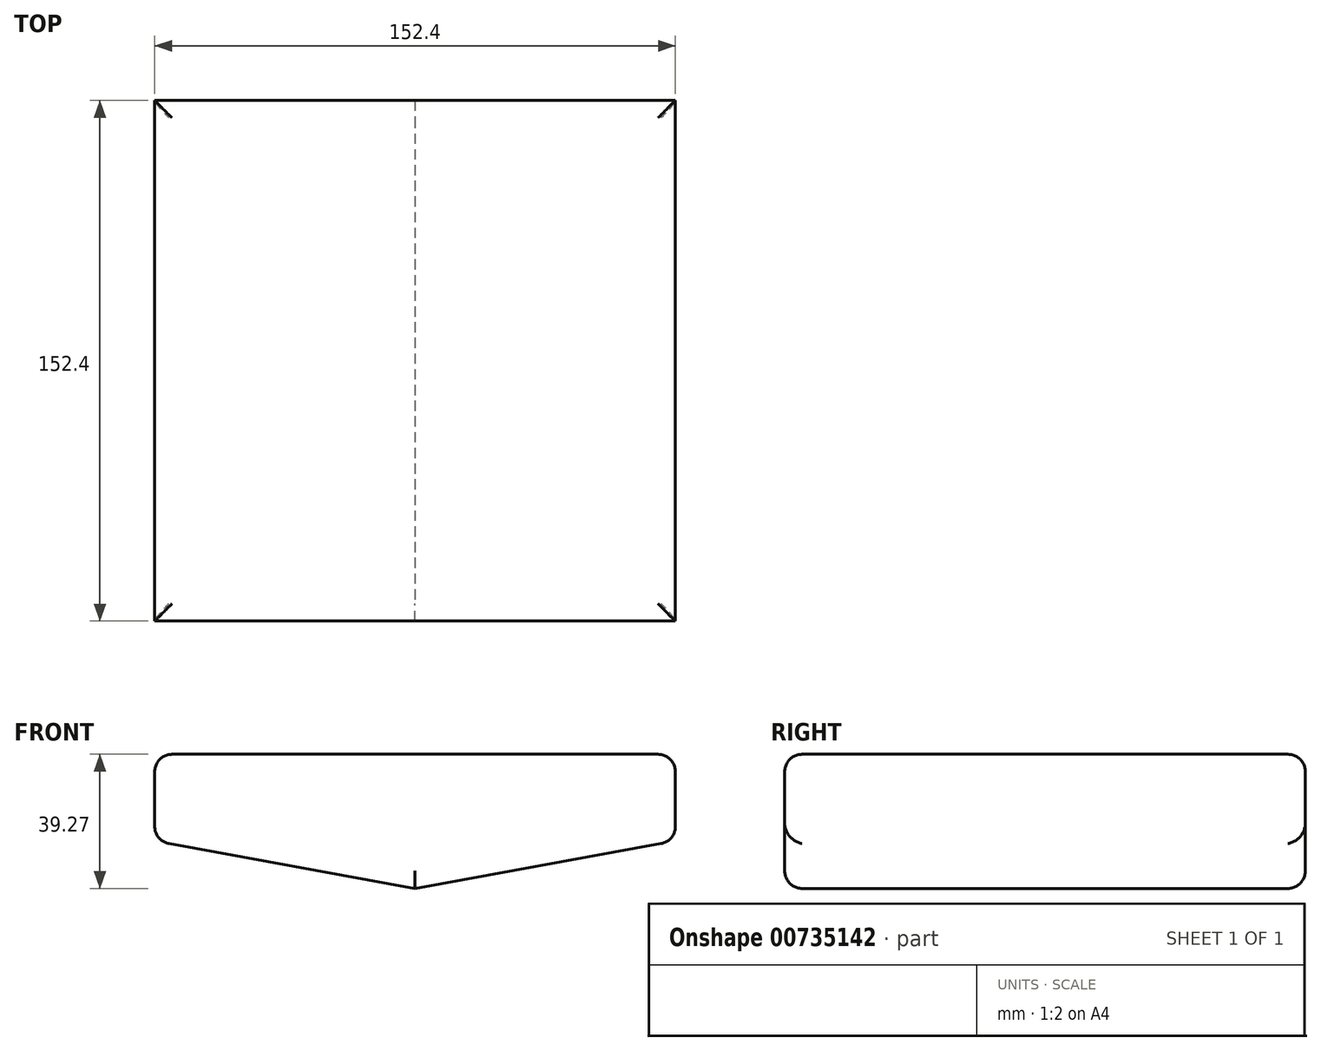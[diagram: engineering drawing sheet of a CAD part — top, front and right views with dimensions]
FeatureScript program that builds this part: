
annotation { "Feature Type Name" : "Feature", "Feature Type Description" : "" }
export const myFeature = defineFeature(function(context is Context, id is Id, definition is map)
    precondition{}
    {
        {
            var Q0;
            Q0=qCreatedBy(makeId("Front.planeOp"),FACE);
            var sketch = newSketch(context, id + "F0", { "sketchPlane" : qUnion([Q0])});
            skLineSegment(sketch, "E0", {"start": v(0, 0) * mm, "end": v(-76.2, 0) * mm});
            skLineSegment(sketch, "E1", {"start": v(0, 0) * mm, "end": v(76.2, 0) * mm});
            skLineSegment(sketch, "E2", {"start": v(76.2, 0) * mm, "end": v(76.2, -25.4) * mm});
            skLineSegment(sketch, "E3", {"start": v(-76.2, 0) * mm, "end": v(-76.2, -25.4) * mm});
            skLineSegment(sketch, "E4", {"start": v(-76.2, -25.4) * mm, "end": v(0, -39.27) * mm});
            skLineSegment(sketch, "E5", {"start": v(0, -39.27) * mm, "end": v(76.2, -25.4) * mm});
            skSolve(sketch);
        }
        {
            var Q0;
            Q0=makeQuery(id+"F0.imprint","IMPRINT",FACE,{"disambiguationData":[TD([[makeQuery(id+"F0.imprint","IMPRINT",EDGE,{"derivedFrom":sQuery(id+"F0.wireOp",EDGE,"E0")}),1.0]])]});
            extrude(context, id + "F1", {"entities" : qUnion([Q0]), "oppositeDirection" : true, "depth" : 152.4 * mm, "offsetDistance" : 25.4 * mm});
        }
        {
            var Q0;
            Q0=makeQuery(id+"F1.opExtrude","SWEPT_FACE",FACE,{"disambiguationData":[OSD([sQuery(id+"F0.wireOp",EDGE,"E0"),sQuery(id+"F0.wireOp",EDGE,"E1")])]});
            fillet(context, id + "F2", {"entities" : qUnion([Q0]), "radius" : 5.08 * mm, "tangentPropagation" : true, "allowEdgeOverflow" : false});
        }
        {
            var Q0;
            Q0=makeQuery(id+"F1.opExtrude","SWEPT_EDGE",EDGE,{"disambiguationData":[OSD([sQuery(id+"F0.wireOp",EDGE,"E2"),sQuery(id+"F0.wireOp",EDGE,"E5")])]});
            var Q1;
            Q1=makeQuery(id+"F1.opExtrude","CAP_EDGE",EDGE,{"disambiguationData":[OSD([sQuery(id+"F0.wireOp",EDGE,"E5")])],"isStart":true});
            var Q2;
            Q2=makeQuery(id+"F1.opExtrude","CAP_EDGE",EDGE,{"disambiguationData":[OSD([sQuery(id+"F0.wireOp",EDGE,"E4")])],"isStart":true});
            var Q3;
            Q3=makeQuery(id+"F1.opExtrude","CAP_EDGE",EDGE,{"disambiguationData":[OSD([sQuery(id+"F0.wireOp",EDGE,"E5")])],"isStart":false});
            var Q4;
            Q4=makeQuery(id+"F1.opExtrude","CAP_EDGE",EDGE,{"disambiguationData":[OSD([sQuery(id+"F0.wireOp",EDGE,"E4")])],"isStart":false});
            var Q5;
            Q5=makeQuery(id+"F1.opExtrude","SWEPT_EDGE",EDGE,{"disambiguationData":[OSD([sQuery(id+"F0.wireOp",EDGE,"E3"),sQuery(id+"F0.wireOp",EDGE,"E4")])]});
            fillet(context, id + "F3", {"entities" : qUnion([Q0, Q1, Q2, Q3, Q4, Q5]), "radius" : 5.08 * mm, "tangentPropagation" : true, "allowEdgeOverflow" : false});
        }
    });
